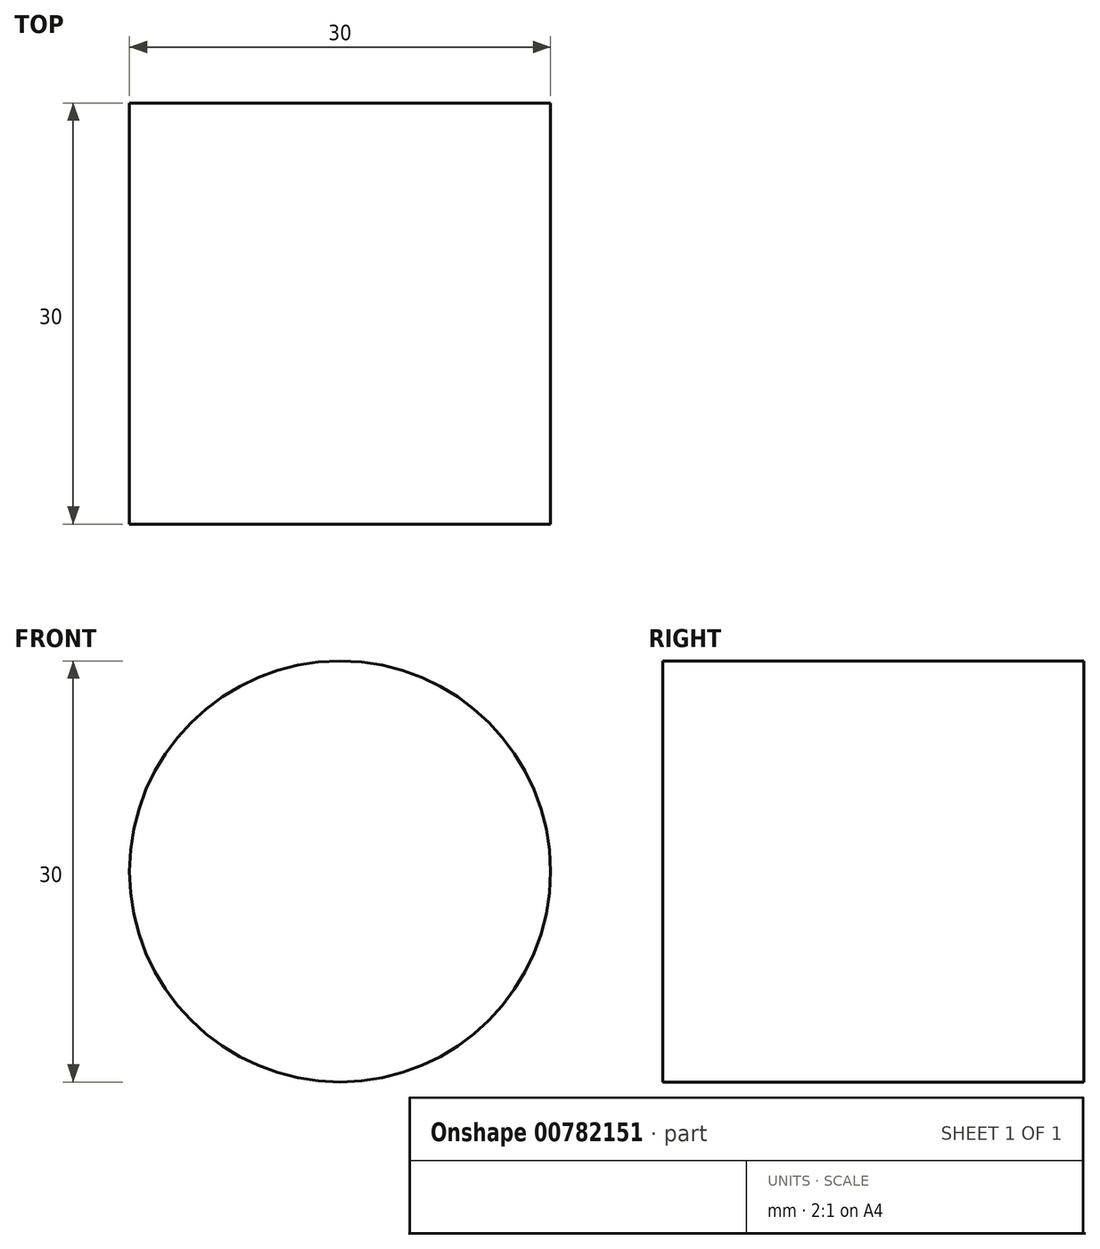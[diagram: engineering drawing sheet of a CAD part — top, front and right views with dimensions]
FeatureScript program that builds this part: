
annotation { "Feature Type Name" : "Feature", "Feature Type Description" : "" }
export const myFeature = defineFeature(function(context is Context, id is Id, definition is map)
    precondition{}
    {
        {
            var Q0;
            Q0=qCreatedBy(makeId("Front.planeOp"),FACE);
            var sketch = newSketch(context, id + "F0", { "sketchPlane" : qUnion([Q0])});
            skCircle(sketch, "E0", {"center": v(0, 0) * mm, "radius": 15 * mm});
            skSolve(sketch);
        }
        {
            var Q0;
            Q0=makeQuery(id+"F0.imprint","IMPRINT",FACE,{"disambiguationData":[TD([[makeQuery(id+"F0.imprint","IMPRINT",EDGE,{"derivedFrom":sQuery(id+"F0.wireOp",EDGE,"E0")}),1.0]])]});
            extrude(context, id + "F1", {"entities" : qUnion([Q0]), "depth" : 30 * mm, "offsetDistance" : 25.4 * mm});
        }
    });
